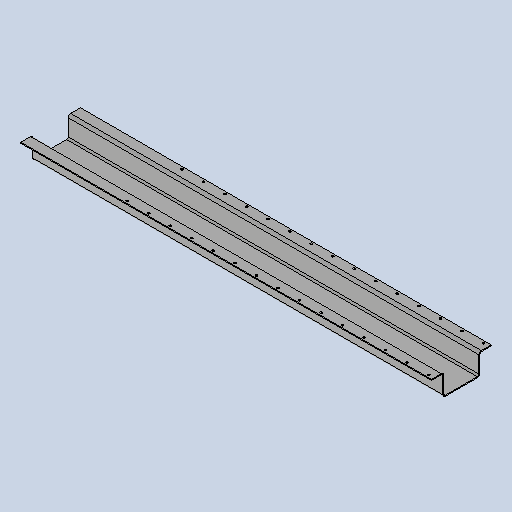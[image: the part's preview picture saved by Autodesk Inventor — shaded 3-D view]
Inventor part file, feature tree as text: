
AUTODESK INVENTOR PART (.ipt)
format: ipt  version: 2025 (Build 290162010, 162A)  size: 242,688 bytes
history: native  units: mm
features: sheet_metal_op x7, other x5, sketch x4, pattern_linear x1, mirror x1
ambient origin geometry x8: Origin, YZ Plane, XZ Plane, XY Plane, X Axis, Y Axis, Z Axis, Center Point
bodies: Solid1 (feature_tree)
feature tree (18):
  sheet_metal_op  "Face1"
  sheet_metal_op  "Flange4"
  sheet_metal_op  "Flange5"
  pattern_linear  "Rectangular Pattern2"  Count1=12  [1 undecoded]
  mirror  "Mirror2"
  sketch  "Sketch1"  dims[d5=1335.0mm]
  other  "Plate1"
  sketch  "Sketch6"  dims[d6=3.0mm d30=120.0mm]
  other  "Plate5"
  sheet_metal_op  "Bend4"
  sheet_metal_op  "Corner4"
  sketch  "Sketch9"  dims[d60=3.0mm]
  other  "Plate6"
  sheet_metal_op  "Bend5"
  sheet_metal_op  "Corner5"
  sketch  "Sketch11"  dims[d61=1.5mm d62=6.0mm d63=5.0mm d64=70.0mm d65=90.0deg d66=5.0mm d67=12.0mm d68=3.0mm d69=5.0mm d81=3.0mm d82=1.5mm d83=6.0mm d84=5.0mm d85=40.0mm d86=90.0deg d87=5.0mm d88=12.0mm d89=3.0mm d90=5.0mm d102=7.0mm d112=3.0mm d113=0.0mm d114=150.0mm d116=70.0mm d132=8.0mm d133=17.0mm]
  other  "Cut1"
  other  "Definition1"
note: 1 required parameter value undecoded (feature->parameter linkage not recoverable at this tier; creation-order binding heuristic only, values carry confidence <= 0.55)
